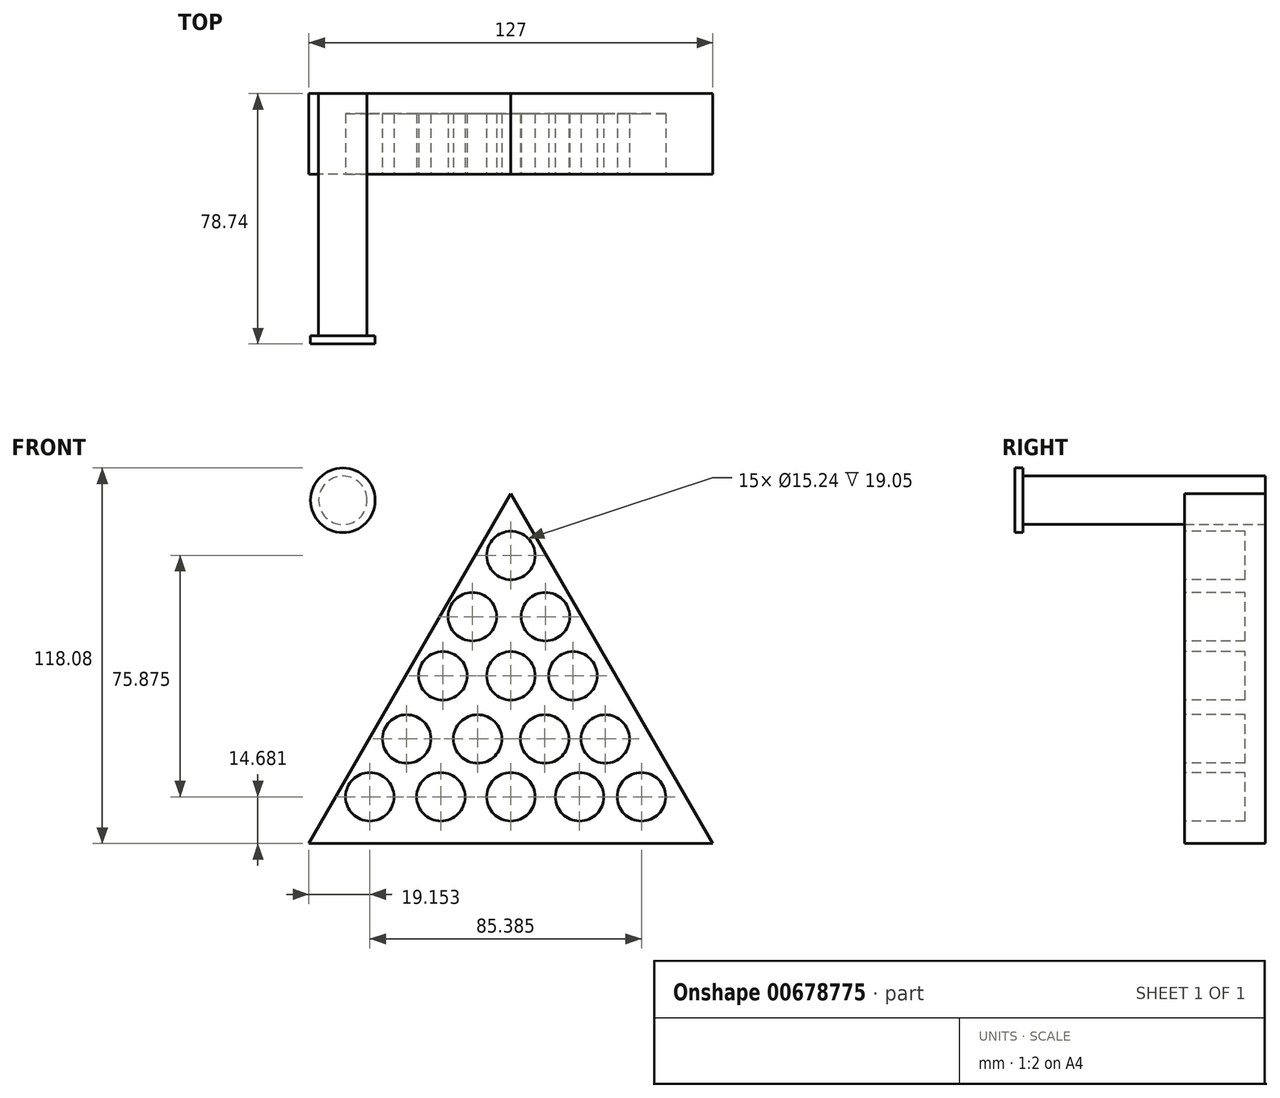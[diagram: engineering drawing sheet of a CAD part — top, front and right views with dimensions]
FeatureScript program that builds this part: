
annotation { "Feature Type Name" : "Feature", "Feature Type Description" : "" }
export const myFeature = defineFeature(function(context is Context, id is Id, definition is map)
    precondition{}
    {
        {
            var Q0;
            Q0=qCreatedBy(makeId("Front.planeOp"),FACE);
            var sketch = newSketch(context, id + "F0", { "sketchPlane" : qUnion([Q0])});
            skLineSegment(sketch, "E0", {"start": v(0, 62.54) * mm, "end": v(-63.5, -47.45) * mm});
            skLineSegment(sketch, "E1", {"start": v(-63.5, -47.45) * mm, "end": v(63.5, -47.45) * mm});
            skLineSegment(sketch, "E2", {"start": v(63.5, -47.45) * mm, "end": v(0, 62.54) * mm});
            skSolve(sketch);
        }
        {
            var Q0;
            Q0 = qSketchRegion(id + "F0", true);
            extrude(context, id + "F1", {"entities" : qUnion([Q0]), "depth" : 25.4 * mm, "offsetDistance" : 25.4 * mm});
        }
        {
            var Q0;
            Q0=makeQuery(id+"F1.opExtrude","CAP_FACE",FACE,{"disambiguationData":[OSD([sQuery(id+"F0.wireOp",EDGE,"E0"),sQuery(id+"F0.wireOp",EDGE,"E1"),sQuery(id+"F0.wireOp",EDGE,"E2")])],"isStart":false});
            var sketch = newSketch(context, id + "F2", { "sketchPlane" : qUnion([Q0])});
            skCircle(sketch, "E3", {"center": v(0, 43.1) * mm, "radius": 7.62 * mm});
            skCircle(sketch, "E4", {"center": v(-12.1, 23.88) * mm, "radius": 7.62 * mm});
            skCircle(sketch, "E5", {"center": v(10.85, 23.88) * mm, "radius": 7.62 * mm});
            skCircle(sketch, "E6", {"center": v(0, 5.27) * mm, "radius": 7.62 * mm});
            skCircle(sketch, "E7", {"center": v(-21.4, 5.27) * mm, "radius": 7.62 * mm});
            skCircle(sketch, "E8", {"center": v(19.54, 5.27) * mm, "radius": 7.62 * mm});
            skCircle(sketch, "E9", {"center": v(-32.77, -14.58) * mm, "radius": 7.62 * mm});
            skCircle(sketch, "E10", {"center": v(-10.44, -14.58) * mm, "radius": 7.62 * mm});
            skCircle(sketch, "E11", {"center": v(10.65, -14.58) * mm, "radius": 7.62 * mm});
            skCircle(sketch, "E12", {"center": v(29.67, -14.58) * mm, "radius": 7.62 * mm});
            skCircle(sketch, "E13", {"center": v(0, -32.77) * mm, "radius": 7.62 * mm});
            skCircle(sketch, "E14", {"center": v(21.6, -32.77) * mm, "radius": 7.62 * mm});
            skCircle(sketch, "E15", {"center": v(41.04, -32.77) * mm, "radius": 7.62 * mm});
            skCircle(sketch, "E16", {"center": v(-22.02, -32.77) * mm, "radius": 7.62 * mm});
            skCircle(sketch, "E17", {"center": v(-44.35, -32.77) * mm, "radius": 7.62 * mm});
            skSolve(sketch);
        }
        {
            var Q0;
            Q0 = qSketchRegion(id + "F2", true);
            extrude(context, id + "F3", {"entities" : qUnion([Q0]), "operationType" : NewBodyOperationType.REMOVE, "oppositeDirection" : true, "depth" : 19.05 * mm, "offsetDistance" : 25.4 * mm});
        }
        {
            var Q0;
            Q0=qCreatedBy(makeId("Front.planeOp"),FACE);
            var sketch = newSketch(context, id + "F4", { "sketchPlane" : qUnion([Q0])});
            skCircle(sketch, "E18", {"center": v(-52.82, 60.47) * mm, "radius": 7.62 * mm});
            skSolve(sketch);
        }
        {
            var Q0;
            Q0 = qSketchRegion(id + "F4", true);
            extrude(context, id + "F5", {"entities" : qUnion([Q0]), "depth" : 76.2 * mm, "offsetDistance" : 25.4 * mm});
        }
        {
            var Q0;
            Q0=makeQuery(id+"F5.opExtrude","CAP_FACE",FACE,{"disambiguationData":[OSD([sQuery(id+"F4.wireOp",EDGE,"E18")])],"isStart":false});
            var sketch = newSketch(context, id + "F6", { "sketchPlane" : qUnion([Q0])});
            skCircle(sketch, "E19", {"center": v(-52.82, 60.47) * mm, "radius": 10.16 * mm});
            skSolve(sketch);
        }
        {
            var Q0;
            Q0=makeQuery(id+"F6.imprint","IMPRINT",FACE,{"disambiguationData":[TD([[makeQuery(id+"F6.imprint","IMPRINT",EDGE,{"derivedFrom":makeQuery(id+"F5.opExtrude","CAP_EDGE",EDGE,{"disambiguationData":[OSD([sQuery(id+"F4.wireOp",EDGE,"E18")])],"isStart":false})}),1.0]])]});
            var Q1;
            Q1 = qSketchRegion(id + "F6", true);
            extrude(context, id + "F7", {"entities" : qUnion([Q0, Q1]), "operationType" : NewBodyOperationType.ADD, "depth" : 2.54 * mm, "offsetDistance" : 25.4 * mm});
        }
    });
